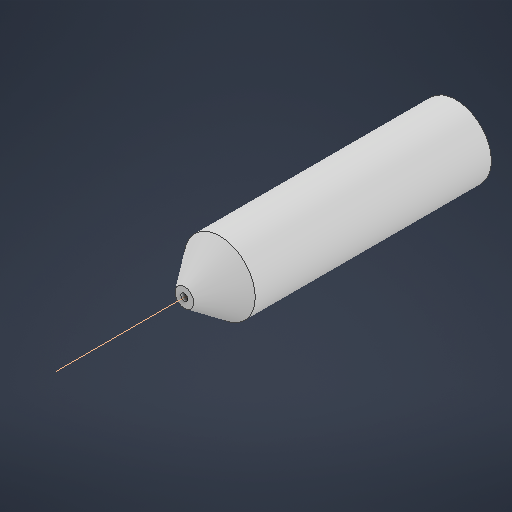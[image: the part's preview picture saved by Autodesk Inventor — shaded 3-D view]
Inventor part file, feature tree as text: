
AUTODESK INVENTOR PART (.ipt)
format: ipt  version: 2025.3 (Build 293356030, 356C)  size: 208,384 bytes
history: native  units: mm
features: sketch x2, extrude x1, revolve x1, other x1
ambient origin geometry x8: Origin, YZ Plane, XZ Plane, XY Plane, X Axis, Y Axis, Z Axis, Center Point
bodies: Solid1 (feature_tree)
feature tree (5):
  extrude  "Extrusion1"  Depth=4.0mm
  revolve  "Revolution1"  [1 undecoded]
  other  "Work Axis1"
  sketch  "Sketch1"  dims[d0=6.0mm d1=4.0mm]
  sketch  "Sketch2"  dims[d2=20.0mm d3=0.0mm d4=3.0mm d6=0.3mm d7=0.5mm d8=90.0deg d5=0.872665mm]
note: 1 required parameter value undecoded (feature->parameter linkage not recoverable at this tier; creation-order binding heuristic only, values carry confidence <= 0.55)
